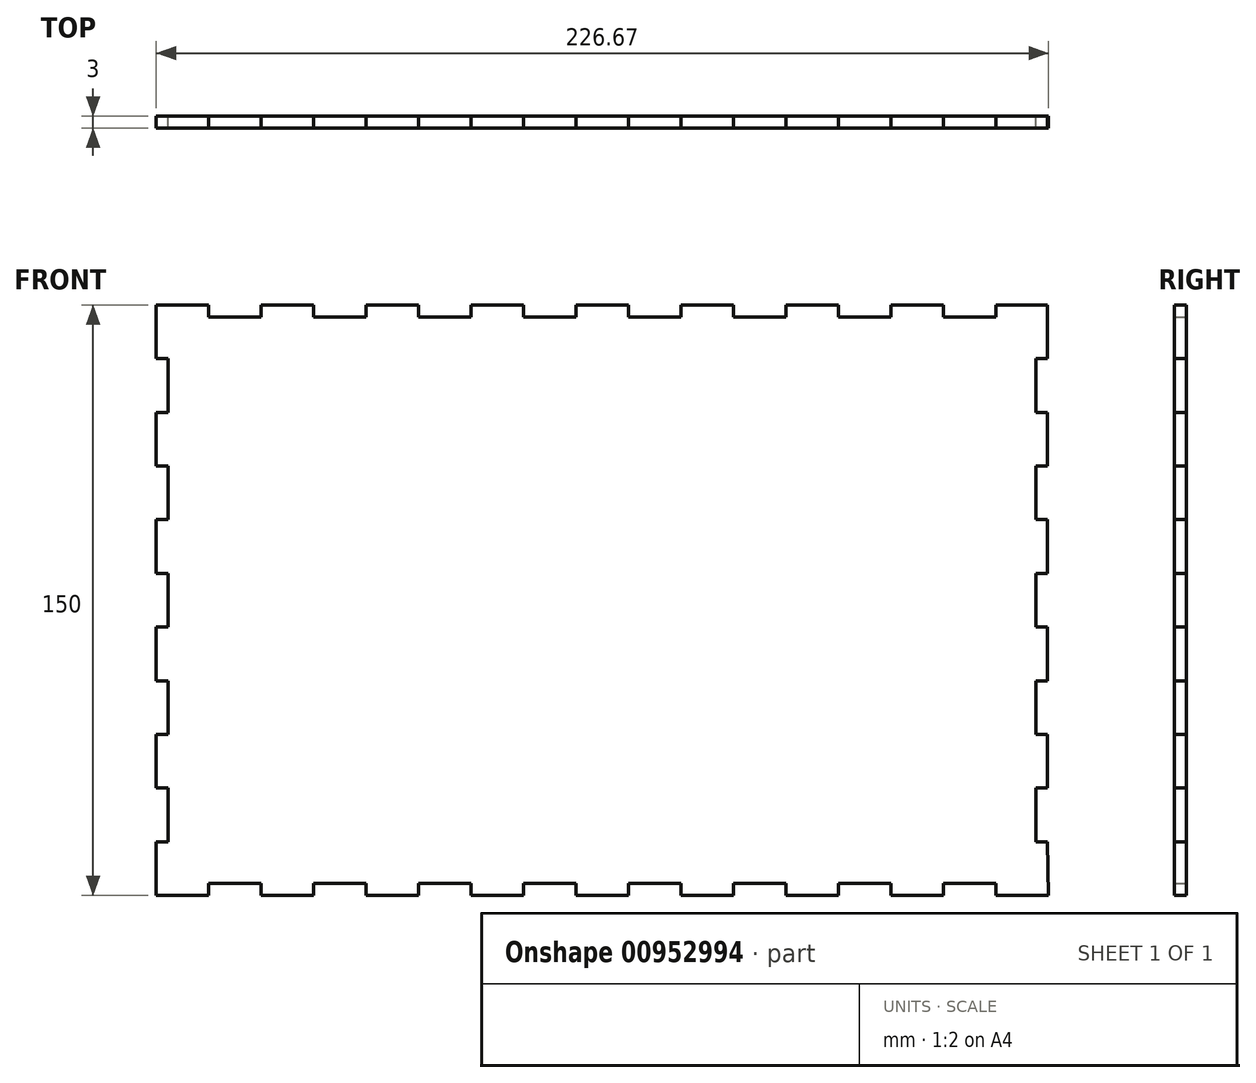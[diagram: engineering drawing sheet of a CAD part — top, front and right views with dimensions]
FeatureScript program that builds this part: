
annotation { "Feature Type Name" : "Feature", "Feature Type Description" : "" }
export const myFeature = defineFeature(function(context is Context, id is Id, definition is map)
    precondition{}
    {
        {
            var Q0;
            Q0=qCreatedBy(makeId("Front.planeOp"),FACE);
            var sketch = newSketch(context, id + "F0", { "sketchPlane" : qUnion([Q0])});
            skLineSegment(sketch, "E0.top", {"start": v(113.24, 75) * mm, "end": v(100.1, 75) * mm});
            skLineSegment(sketch, "E0.right", {"start": v(-113.24, -75) * mm, "end": v(-113.24, -61.36) * mm});
            skPoint(sketch, "E0.middle", {"position": v(0, 0) * mm});
            skLineSegment(sketch, "E1", {"start": v(-99.9, 72) * mm, "end": v(-86.57, 72) * mm});
            skLineSegment(sketch, "E2", {"start": v(-99.9, 75) * mm, "end": v(-99.9, 72) * mm});
            skLineSegment(sketch, "E3", {"start": v(-86.57, 75) * mm, "end": v(-86.57, 72) * mm});
            skLineSegment(sketch, "E4", {"start": v(-73.24, 75) * mm, "end": v(-73.24, 72) * mm});
            skLineSegment(sketch, "E5", {"start": v(-59.9, 75) * mm, "end": v(-59.9, 72) * mm});
            skLineSegment(sketch, "E6", {"start": v(-46.57, 75) * mm, "end": v(-46.57, 72) * mm});
            skLineSegment(sketch, "E7", {"start": v(-33.24, 75) * mm, "end": v(-33.24, 72) * mm});
            skLineSegment(sketch, "E8", {"start": v(-19.9, 75) * mm, "end": v(-19.9, 72) * mm});
            skLineSegment(sketch, "E9", {"start": v(-6.57, 75) * mm, "end": v(-6.57, 72) * mm});
            skLineSegment(sketch, "E10", {"start": v(6.76, 75) * mm, "end": v(6.76, 72) * mm});
            skLineSegment(sketch, "E11", {"start": v(20.1, 75) * mm, "end": v(20.1, 72) * mm});
            skLineSegment(sketch, "E12", {"start": v(33.43, 75) * mm, "end": v(33.43, 72) * mm});
            skLineSegment(sketch, "E13", {"start": v(46.76, 75) * mm, "end": v(46.76, 72) * mm});
            skLineSegment(sketch, "E14", {"start": v(60.1, 75) * mm, "end": v(60.1, 72) * mm});
            skLineSegment(sketch, "E15", {"start": v(73.43, 75) * mm, "end": v(73.43, 72) * mm});
            skLineSegment(sketch, "E16.trimOffspring", {"start": v(-99.9, 75) * mm, "end": v(-113.24, 75) * mm});
            skLineSegment(sketch, "E17.trimOffspring", {"start": v(-73.24, 72) * mm, "end": v(-59.9, 72) * mm});
            skLineSegment(sketch, "E18.trimOffspring", {"start": v(-73.24, 75) * mm, "end": v(-86.57, 75) * mm});
            skLineSegment(sketch, "E19.trimOffspring", {"start": v(-46.57, 72) * mm, "end": v(-33.24, 72) * mm});
            skLineSegment(sketch, "E20.trimOffspring", {"start": v(-46.57, 75) * mm, "end": v(-59.9, 75) * mm});
            skLineSegment(sketch, "E21.trimOffspring", {"start": v(-19.9, 72) * mm, "end": v(-6.57, 72) * mm});
            skLineSegment(sketch, "E22.trimOffspring", {"start": v(-19.9, 75) * mm, "end": v(-33.24, 75) * mm});
            skLineSegment(sketch, "E23.trimOffspring", {"start": v(6.76, 72) * mm, "end": v(20.1, 72) * mm});
            skLineSegment(sketch, "E24.trimOffspring", {"start": v(6.76, 75) * mm, "end": v(-6.57, 75) * mm});
            skLineSegment(sketch, "E25.trimOffspring", {"start": v(33.43, 72) * mm, "end": v(46.76, 72) * mm});
            skLineSegment(sketch, "E26.trimOffspring", {"start": v(33.43, 75) * mm, "end": v(20.1, 75) * mm});
            skLineSegment(sketch, "E27.trimOffspring", {"start": v(60.1, 72) * mm, "end": v(73.43, 72) * mm});
            skLineSegment(sketch, "E28.trimOffspring", {"start": v(60.1, 75) * mm, "end": v(46.76, 75) * mm});
            skLineSegment(sketch, "E29", {"start": v(-110.24, 61.36) * mm, "end": v(-110.24, 47.73) * mm});
            skLineSegment(sketch, "E30", {"start": v(-113.24, 61.36) * mm, "end": v(-110.24, 61.36) * mm});
            skLineSegment(sketch, "E31", {"start": v(-113.24, 47.73) * mm, "end": v(-110.24, 47.73) * mm});
            skLineSegment(sketch, "E32", {"start": v(-113.24, 34.1) * mm, "end": v(-110.24, 34.1) * mm});
            skLineSegment(sketch, "E33", {"start": v(-113.24, 20.45) * mm, "end": v(-110.24, 20.45) * mm});
            skLineSegment(sketch, "E34", {"start": v(-113.24, 6.82) * mm, "end": v(-110.24, 6.82) * mm});
            skLineSegment(sketch, "E35", {"start": v(-113.24, -6.82) * mm, "end": v(-110.24, -6.82) * mm});
            skLineSegment(sketch, "E36", {"start": v(-113.24, -34.1) * mm, "end": v(-110.24, -34.1) * mm});
            skLineSegment(sketch, "E37", {"start": v(-113.24, -61.36) * mm, "end": v(-110.24, -61.36) * mm});
            skLineSegment(sketch, "E38", {"start": v(-113.24, -20.45) * mm, "end": v(-110.24, -20.45) * mm});
            skLineSegment(sketch, "E39", {"start": v(-113.24, -47.73) * mm, "end": v(-110.24, -47.73) * mm});
            skLineSegment(sketch, "E40.trimOffspring", {"start": v(-113.24, 61.36) * mm, "end": v(-113.24, 75) * mm});
            skLineSegment(sketch, "E41.trimOffspring", {"start": v(-110.24, 34.1) * mm, "end": v(-110.24, 20.45) * mm});
            skLineSegment(sketch, "E42.trimOffspring", {"start": v(-113.24, 34.1) * mm, "end": v(-113.24, 47.73) * mm});
            skLineSegment(sketch, "E43.trimOffspring", {"start": v(-110.24, 6.82) * mm, "end": v(-110.24, -6.82) * mm});
            skLineSegment(sketch, "E44.trimOffspring", {"start": v(-113.24, 6.82) * mm, "end": v(-113.24, 20.45) * mm});
            skLineSegment(sketch, "E45.trimOffspring", {"start": v(-110.24, -20.45) * mm, "end": v(-110.24, -34.1) * mm});
            skLineSegment(sketch, "E46.trimOffspring", {"start": v(-113.24, -20.45) * mm, "end": v(-113.24, -6.82) * mm});
            skLineSegment(sketch, "E47.trimOffspring", {"start": v(-110.24, -47.73) * mm, "end": v(-110.24, -61.36) * mm});
            skLineSegment(sketch, "E48.trimOffspring", {"start": v(-113.24, -47.73) * mm, "end": v(-113.24, -34.1) * mm});
            skLineSegment(sketch, "E49.MirrorCS", {"start": v(113.24, 47.73) * mm, "end": v(110.24, 47.73) * mm});
            skLineSegment(sketch, "E50.MirrorCS", {"start": v(113.24, 34.1) * mm, "end": v(110.24, 34.1) * mm});
            skLineSegment(sketch, "E51.MirrorCS", {"start": v(113.24, 20.45) * mm, "end": v(110.24, 20.45) * mm});
            skLineSegment(sketch, "E52.MirrorCS", {"start": v(113.24, 61.36) * mm, "end": v(110.24, 61.36) * mm});
            skLineSegment(sketch, "E53.MirrorCS", {"start": v(113.24, 6.82) * mm, "end": v(110.24, 6.82) * mm});
            skLineSegment(sketch, "E54.MirrorCS", {"start": v(113.24, -61.36) * mm, "end": v(110.24, -61.36) * mm});
            skLineSegment(sketch, "E55.MirrorCS", {"start": v(113.24, -20.45) * mm, "end": v(110.24, -20.45) * mm});
            skLineSegment(sketch, "E56.MirrorCS", {"start": v(113.24, -47.73) * mm, "end": v(110.24, -47.73) * mm});
            skLineSegment(sketch, "E57.MirrorCS", {"start": v(113.24, -34.1) * mm, "end": v(110.24, -34.1) * mm});
            skLineSegment(sketch, "E58.MirrorCS", {"start": v(113.24, -6.82) * mm, "end": v(110.24, -6.82) * mm});
            skLineSegment(sketch, "E59.MirrorCS", {"start": v(113.24, -20.45) * mm, "end": v(113.24, -6.82) * mm});
            skLineSegment(sketch, "E60.MirrorCS", {"start": v(113.24, 34.1) * mm, "end": v(113.24, 47.73) * mm});
            skLineSegment(sketch, "E61.MirrorCS", {"start": v(113.24, 6.82) * mm, "end": v(113.24, 20.45) * mm});
            skLineSegment(sketch, "E62.MirrorCS", {"start": v(113.24, -47.73) * mm, "end": v(113.24, -34.1) * mm});
            skLineSegment(sketch, "E63.MirrorCS", {"start": v(110.24, 61.36) * mm, "end": v(110.24, 47.73) * mm});
            skLineSegment(sketch, "E64.MirrorCS", {"start": v(110.24, -20.45) * mm, "end": v(110.24, -34.1) * mm});
            skLineSegment(sketch, "E65.MirrorCS", {"start": v(110.24, 6.82) * mm, "end": v(110.24, -6.82) * mm});
            skLineSegment(sketch, "E66.MirrorCS", {"start": v(110.24, -47.73) * mm, "end": v(110.24, -61.36) * mm});
            skLineSegment(sketch, "E67.MirrorCS", {"start": v(110.24, 34.1) * mm, "end": v(110.24, 20.45) * mm});
            skPoint(sketch, "E68.MirrorCS.end.orphan", {"position": v(113.24, 75) * mm});
            skLineSegment(sketch, "E69.top", {"start": v(113.43, 75) * mm, "end": v(100.1, 75) * mm});
            skLineSegment(sketch, "E70", {"start": v(86.76, 75) * mm, "end": v(86.76, 72) * mm});
            skLineSegment(sketch, "E71", {"start": v(100.1, 75) * mm, "end": v(100.1, 72) * mm});
            skLineSegment(sketch, "E72.trimOffspring", {"start": v(86.76, 72) * mm, "end": v(100.1, 72) * mm});
            skLineSegment(sketch, "E73.MirrorCS", {"start": v(86.76, -75) * mm, "end": v(86.76, -72) * mm});
            skLineSegment(sketch, "E74.MirrorCS", {"start": v(60.1, -75) * mm, "end": v(60.1, -72) * mm});
            skLineSegment(sketch, "E75.MirrorCS", {"start": v(46.76, -75) * mm, "end": v(46.76, -72) * mm});
            skLineSegment(sketch, "E76.MirrorCS", {"start": v(-59.9, -75) * mm, "end": v(-59.9, -72) * mm});
            skLineSegment(sketch, "E77.MirrorCS", {"start": v(-33.24, -75) * mm, "end": v(-33.24, -72) * mm});
            skLineSegment(sketch, "E78.MirrorCS", {"start": v(-6.57, -75) * mm, "end": v(-6.57, -72) * mm});
            skLineSegment(sketch, "E79.MirrorCS", {"start": v(33.43, -75) * mm, "end": v(33.43, -72) * mm});
            skLineSegment(sketch, "E80.MirrorCS", {"start": v(-99.9, -75) * mm, "end": v(-99.9, -72) * mm});
            skLineSegment(sketch, "E81.MirrorCS", {"start": v(20.1, -75) * mm, "end": v(20.1, -72) * mm});
            skLineSegment(sketch, "E82.MirrorCS", {"start": v(100.1, -75) * mm, "end": v(100.1, -72) * mm});
            skLineSegment(sketch, "E83.MirrorCS", {"start": v(-19.9, -75) * mm, "end": v(-19.9, -72) * mm});
            skLineSegment(sketch, "E84.MirrorCS", {"start": v(6.76, -75) * mm, "end": v(6.76, -72) * mm});
            skLineSegment(sketch, "E85.MirrorCS", {"start": v(73.43, -75) * mm, "end": v(73.43, -72) * mm});
            skLineSegment(sketch, "E86.MirrorCS", {"start": v(-73.24, -75) * mm, "end": v(-73.24, -72) * mm});
            skLineSegment(sketch, "E87.MirrorCS", {"start": v(-46.57, -75) * mm, "end": v(-46.57, -72) * mm});
            skLineSegment(sketch, "E88.MirrorCS", {"start": v(-86.57, -75) * mm, "end": v(-86.57, -72) * mm});
            skLineSegment(sketch, "E89.MirrorCS", {"start": v(33.43, -72) * mm, "end": v(46.76, -72) * mm});
            skLineSegment(sketch, "E90.MirrorCS", {"start": v(-19.9, -75) * mm, "end": v(-33.24, -75) * mm});
            skLineSegment(sketch, "E91.MirrorCS", {"start": v(33.43, -75) * mm, "end": v(20.1, -75) * mm});
            skLineSegment(sketch, "E92.MirrorCS", {"start": v(-99.9, -75) * mm, "end": v(-113.24, -75) * mm});
            skLineSegment(sketch, "E93.MirrorCS", {"start": v(-46.57, -75) * mm, "end": v(-59.9, -75) * mm});
            skLineSegment(sketch, "E94.MirrorCS", {"start": v(113.24, -75) * mm, "end": v(100.1, -75) * mm});
            skLineSegment(sketch, "E95.MirrorCS", {"start": v(-19.9, -72) * mm, "end": v(-6.57, -72) * mm});
            skPoint(sketch, "E96.MirrorP", {"position": v(113.24, -75) * mm});
            skLineSegment(sketch, "E97.MirrorCS", {"start": v(60.1, -75) * mm, "end": v(46.76, -75) * mm});
            skLineSegment(sketch, "E98.MirrorCS", {"start": v(60.1, -72) * mm, "end": v(73.43, -72) * mm});
            skLineSegment(sketch, "E99.MirrorCS", {"start": v(-46.57, -72) * mm, "end": v(-33.24, -72) * mm});
            skLineSegment(sketch, "E100.MirrorCS", {"start": v(-73.24, -75) * mm, "end": v(-86.57, -75) * mm});
            skLineSegment(sketch, "E101.MirrorCS", {"start": v(-73.24, -72) * mm, "end": v(-59.9, -72) * mm});
            skLineSegment(sketch, "E102.MirrorCS", {"start": v(-99.9, -72) * mm, "end": v(-86.57, -72) * mm});
            skLineSegment(sketch, "E103.MirrorCS", {"start": v(6.76, -72) * mm, "end": v(20.1, -72) * mm});
            skLineSegment(sketch, "E104.MirrorCS", {"start": v(86.76, -72) * mm, "end": v(100.1, -72) * mm});
            skLineSegment(sketch, "E105.MirrorCS", {"start": v(6.76, -75) * mm, "end": v(-6.57, -75) * mm});
            skLineSegment(sketch, "E106.MirrorCS", {"start": v(113.43, -75) * mm, "end": v(100.1, -75) * mm});
            skLineSegment(sketch, "E107", {"start": v(113.24, 75) * mm, "end": v(113.24, 61.36) * mm});
            skLineSegment(sketch, "E108", {"start": v(113.43, -75) * mm, "end": v(113.24, -61.36) * mm});
            skLineSegment(sketch, "E109.trimOffspring", {"start": v(86.76, -75) * mm, "end": v(73.43, -75) * mm});
            skLineSegment(sketch, "E110.trimOffspring", {"start": v(86.76, 75) * mm, "end": v(73.43, 75) * mm});
            skSolve(sketch);
        }
        {
            var Q0;
            Q0=makeQuery(id+"F0.imprint","IMPRINT",FACE,{"disambiguationData":[TD([[makeQuery(id+"F0.imprint","IMPRINT",EDGE,{"derivedFrom":sQuery(id+"F0.wireOp",EDGE,"E0.right")}),-1.0]])]});
            extrude(context, id + "F1", {"entities" : qUnion([Q0]), "depth" : 3 * mm, "offsetDistance" : 25 * mm});
        }
    });
